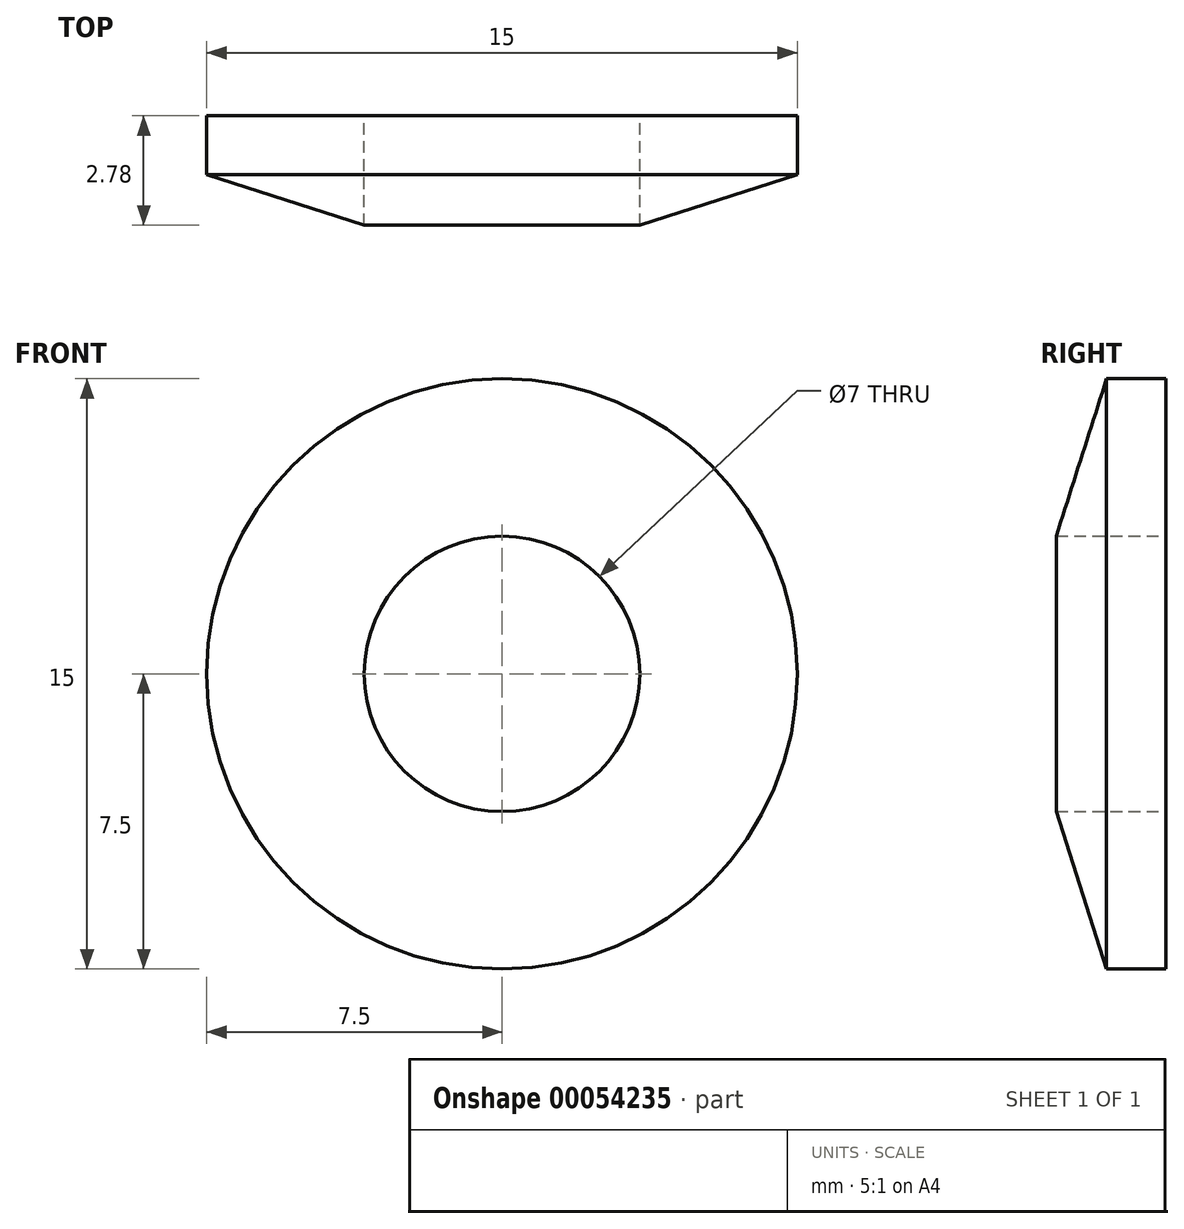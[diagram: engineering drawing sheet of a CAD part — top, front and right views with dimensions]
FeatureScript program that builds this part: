
annotation { "Feature Type Name" : "Feature", "Feature Type Description" : "" }
export const myFeature = defineFeature(function(context is Context, id is Id, definition is map)
    precondition{}
    {
        {
            var Q0;
            Q0=qCreatedBy(makeId("Right.planeOp"),FACE);
            var sketch = newSketch(context, id + "F0", { "sketchPlane" : qUnion([Q0])});
            skLineSegment(sketch, "E0", {"start": v(0, 0) * mm, "end": v(0, -7.5) * mm});
            skLineSegment(sketch, "E1", {"start": v(0, -7.5) * mm, "end": v(-1.5, -7.5) * mm});
            skLineSegment(sketch, "E2", {"start": v(-1.5, -7.5) * mm, "end": v(-2.78, -3.5) * mm});
            skLineSegment(sketch, "E3", {"start": v(-2.78, -3.5) * mm, "end": v(0, -3.5) * mm});
            skLineSegment(sketch, "E4", {"start": v(0, 0) * mm, "end": v(-2.65, 0) * mm});
            skSolve(sketch);
        }
        {
            var Q0;
            Q0 = qSketchRegion(id + "F0", true);
            var Q1;
            {var subQ0=sQuery(id+"F0.wireOp",EDGE,"E1");Q1=makeQuery(id+"F0.imprint","IMPRINT",FACE,{"disambiguationData":[TD([[makeQuery(id+"F0.imprint","IMPRINT",EDGE,{"derivedFrom":subQ0}),-1.0]])]});}
            var Q2;
            Q2=sQuery(id+"F0.wireOp",EDGE,"E4");
            revolve(context, id + "F1", {"entities" : qUnion([Q0, Q1]), "axis" : qUnion([Q2]), "revolveType" : RevolveType.FULL});
        }
    });
